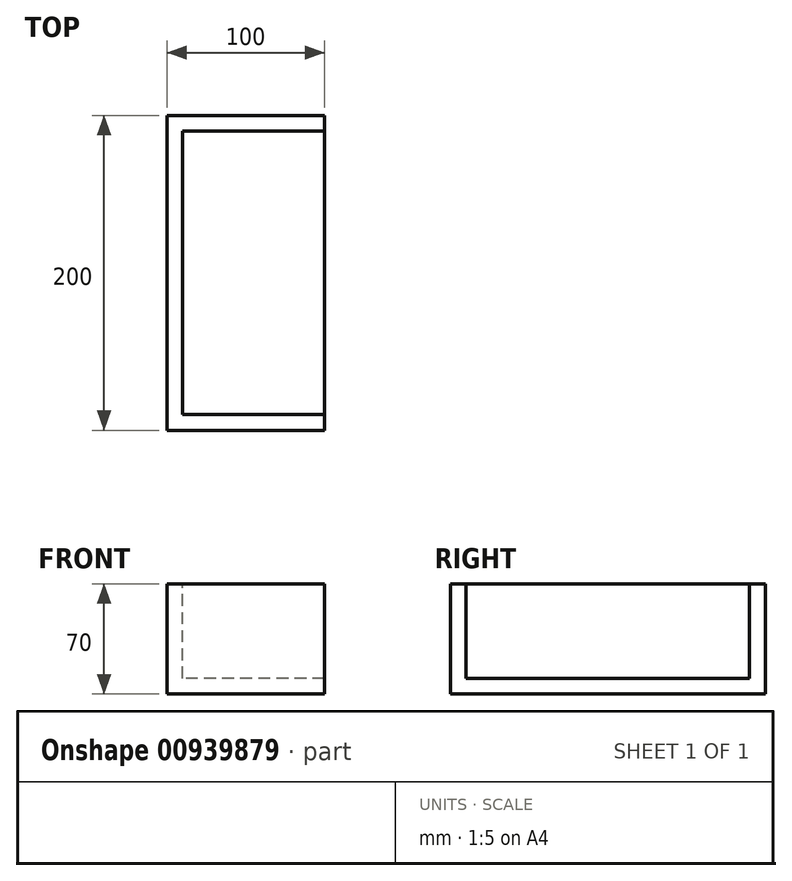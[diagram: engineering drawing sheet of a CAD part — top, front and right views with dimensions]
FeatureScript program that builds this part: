
annotation { "Feature Type Name" : "Feature", "Feature Type Description" : "" }
export const myFeature = defineFeature(function(context is Context, id is Id, definition is map)
    precondition{}
    {
        {
            var Q0;
            Q0=qCreatedBy(makeId("Right.planeOp"),FACE);
            var sketch = newSketch(context, id + "F0", { "sketchPlane" : qUnion([Q0])});
            skLineSegment(sketch, "E0.bottom", {"start": v(100, 35) * mm, "end": v(-100, 35) * mm});
            skLineSegment(sketch, "E0.top", {"start": v(100, -35) * mm, "end": v(-100, -35) * mm});
            skLineSegment(sketch, "E0.left", {"start": v(100, 35) * mm, "end": v(100, -35) * mm});
            skLineSegment(sketch, "E0.right", {"start": v(-100, 35) * mm, "end": v(-100, -35) * mm});
            skPoint(sketch, "E0.middle", {"position": v(0, 0) * mm});
            skSolve(sketch);
        }
        {
            var Q0;
            Q0 = qSketchRegion(id + "F0", true);
            extrude(context, id + "F1", {"entities" : qUnion([Q0]), "depth" : 100 * mm, "offsetDistance" : 25 * mm});
        }
        {
            var Q0;
            Q0=makeQuery(id+"F1.opExtrude","SWEPT_FACE",FACE,{"disambiguationData":[OSD([sQuery(id+"F0.wireOp",EDGE,"E0.bottom")])]});
            var sketch = newSketch(context, id + "F2", { "sketchPlane" : qUnion([Q0])});
            skLineSegment(sketch, "E1.bottom", {"start": v(100, 90) * mm, "end": v(10, 90) * mm});
            skLineSegment(sketch, "E1.top", {"start": v(100, -90) * mm, "end": v(10, -90) * mm});
            skLineSegment(sketch, "E1.left", {"start": v(100, 90) * mm, "end": v(100, -90) * mm});
            skLineSegment(sketch, "E1.right", {"start": v(10, 90) * mm, "end": v(10, -90) * mm});
            skSolve(sketch);
        }
        {
            var Q0;
            Q0 = qSketchRegion(id + "F2", true);
            extrude(context, id + "F3", {"entities" : qUnion([Q0]), "operationType" : NewBodyOperationType.REMOVE, "oppositeDirection" : true, "depth" : 60 * mm, "offsetDistance" : 25 * mm});
        }
    });
